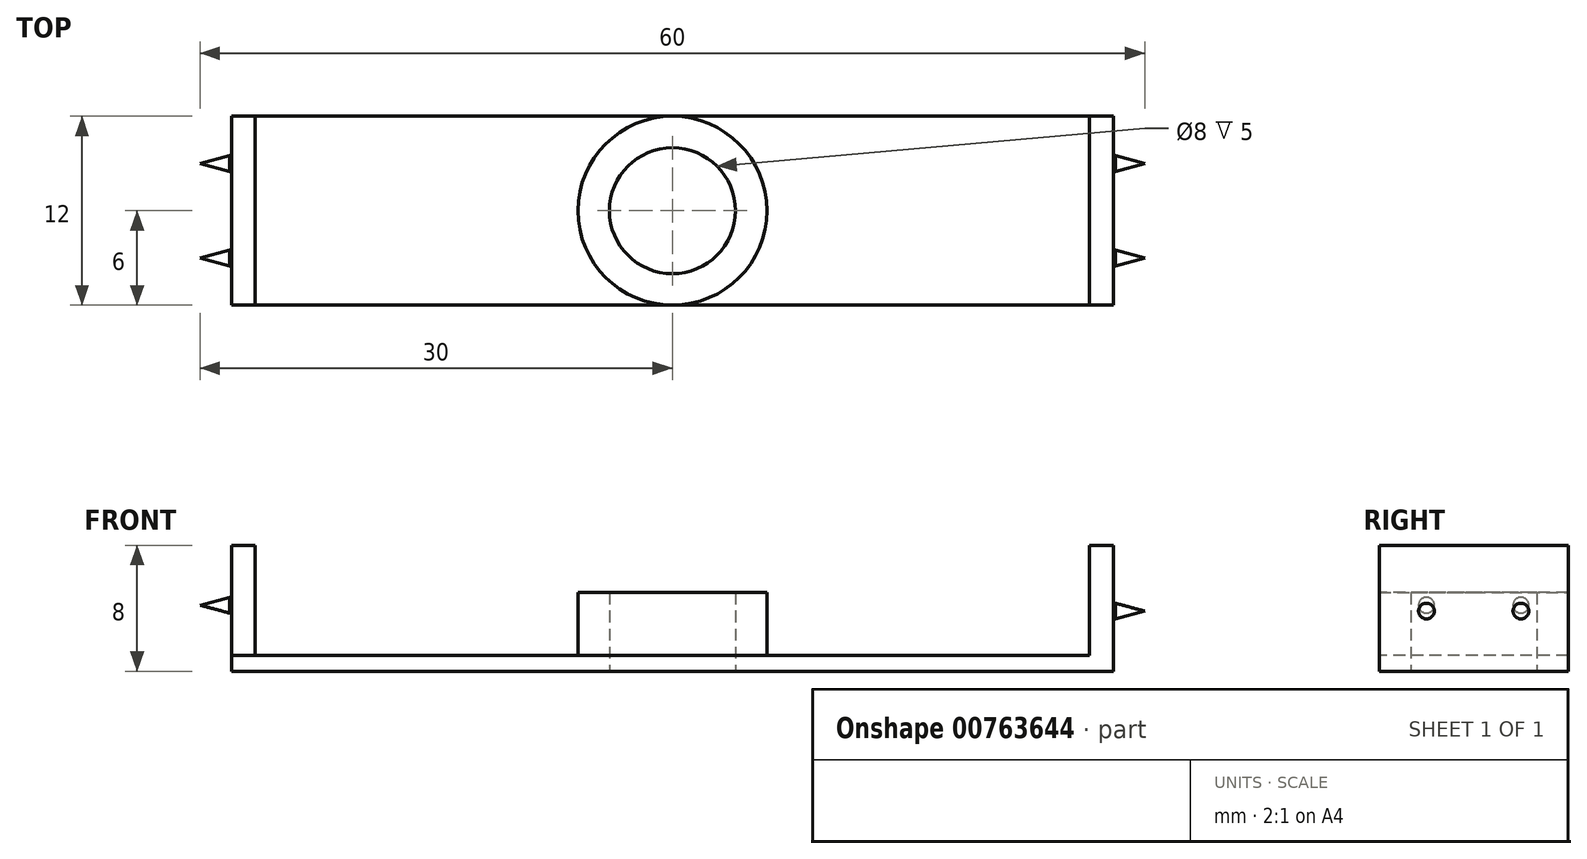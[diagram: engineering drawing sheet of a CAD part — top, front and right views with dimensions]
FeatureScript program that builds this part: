
annotation { "Feature Type Name" : "Feature", "Feature Type Description" : "" }
export const myFeature = defineFeature(function(context is Context, id is Id, definition is map)
    precondition{}
    {
        {
            var Q0;
            Q0=qCreatedBy(makeId("Top.planeOp"),FACE);
            var sketch = newSketch(context, id + "F0", { "sketchPlane" : qUnion([Q0])});
            skLineSegment(sketch, "E0.bottom", {"start": v(-28, 6) * mm, "end": v(28, 6) * mm});
            skLineSegment(sketch, "E0.top", {"start": v(-28, -6) * mm, "end": v(28, -6) * mm});
            skLineSegment(sketch, "E0.left", {"start": v(-28, 6) * mm, "end": v(-28, -6) * mm});
            skLineSegment(sketch, "E0.right", {"start": v(28, 6) * mm, "end": v(28, -6) * mm});
            skSolve(sketch);
        }
        {
            var Q0;
            Q0=makeQuery(id+"F0.imprint","IMPRINT",FACE,{"disambiguationData":[TD([[makeQuery(id+"F0.imprint","IMPRINT",EDGE,{"derivedFrom":sQuery(id+"F0.wireOp",EDGE,"E0.bottom")}),-1.0]])]});
            extrude(context, id + "F1", {"entities" : qUnion([Q0]), "depth" : 1 * mm, "offsetDistance" : 25 * mm});
        }
        {
            var Q0;
            Q0=makeQuery(id+"F1.opExtrude","CAP_FACE",FACE,{"disambiguationData":[OSD([sQuery(id+"F0.wireOp",EDGE,"E0.bottom"),sQuery(id+"F0.wireOp",EDGE,"E0.top"),sQuery(id+"F0.wireOp",EDGE,"E0.left"),sQuery(id+"F0.wireOp",EDGE,"E0.right")])],"isStart":false});
            var sketch = newSketch(context, id + "F2", { "sketchPlane" : qUnion([Q0])});
            skLineSegment(sketch, "E1.bottom", {"start": v(6, -6) * mm, "end": v(-6, -6) * mm});
            skLineSegment(sketch, "E1.top", {"start": v(6, 6) * mm, "end": v(-6, 6) * mm});
            skLineSegment(sketch, "E1.left", {"start": v(6, -6) * mm, "end": v(6, 6) * mm});
            skLineSegment(sketch, "E1.right", {"start": v(-6, -6) * mm, "end": v(-6, 6) * mm});
            skPoint(sketch, "E1.middle", {"position": v(0, 0) * mm});
            skCircle(sketch, "E2", {"center": v(0, 0) * mm, "radius": 4 * mm});
            skSolve(sketch);
        }
        {
            var Q0;
            Q0=makeQuery(id+"F2.imprint","IMPRINT",FACE,{"disambiguationData":[TD([[makeQuery(id+"F2.imprint","IMPRINT",EDGE,{"derivedFrom":sQuery(id+"F2.wireOp",EDGE,"E1.bottom")}),1.0]])]});
            extrude(context, id + "F3", {"entities" : qUnion([Q0]), "operationType" : NewBodyOperationType.ADD, "depth" : 4 * mm, "offsetDistance" : 25 * mm});
        }
        {
            var Q0;
            Q0=makeQuery(id+"F3.boolean.opBoolean","SPLIT",FACE,{"disambiguationData":[TD([makeQuery(id+"F3.opExtrude","SWEPT_FACE",FACE,{"disambiguationData":[OSD([sQuery(id+"F2.wireOp",EDGE,"E2")])]})])],"derivedFrom":makeQuery(id+"F1.opExtrude","CAP_FACE",FACE,{"disambiguationData":[OSD([sQuery(id+"F0.wireOp",EDGE,"E0.bottom"),sQuery(id+"F0.wireOp",EDGE,"E0.top"),sQuery(id+"F0.wireOp",EDGE,"E0.left"),sQuery(id+"F0.wireOp",EDGE,"E0.right")])],"isStart":false})});
            extrude(context, id + "F4", {"entities" : qUnion([Q0]), "operationType" : NewBodyOperationType.REMOVE, "oppositeDirection" : true, "depth" : 25 * mm, "offsetDistance" : 25 * mm});
        }
        {
            var Q0;
            Q0=makeQuery(id+"F3.opExtrude","SWEPT_EDGE",EDGE,{"disambiguationData":[OSD([sQuery(id+"F0.wireOp",EDGE,"E0.bottom"),sQuery(id+"F2.wireOp",EDGE,"E1.top"),sQuery(id+"F2.wireOp",EDGE,"E1.left")])]});
            var Q1;
            Q1=makeQuery(id+"F3.opExtrude","SWEPT_EDGE",EDGE,{"disambiguationData":[OSD([sQuery(id+"F0.wireOp",EDGE,"E0.top"),sQuery(id+"F2.wireOp",EDGE,"E1.bottom"),sQuery(id+"F2.wireOp",EDGE,"E1.left")])]});
            var Q2;
            Q2=makeQuery(id+"F3.opExtrude","SWEPT_EDGE",EDGE,{"disambiguationData":[OSD([sQuery(id+"F0.wireOp",EDGE,"E0.top"),sQuery(id+"F2.wireOp",EDGE,"E1.bottom"),sQuery(id+"F2.wireOp",EDGE,"E1.right")])]});
            var Q3;
            Q3=makeQuery(id+"F3.opExtrude","SWEPT_EDGE",EDGE,{"disambiguationData":[OSD([sQuery(id+"F0.wireOp",EDGE,"E0.bottom"),sQuery(id+"F2.wireOp",EDGE,"E1.top"),sQuery(id+"F2.wireOp",EDGE,"E1.right")])]});
            fillet(context, id + "F5", {"entities" : qUnion([Q0, Q1, Q2, Q3]), "radius" : 6 * mm, "tangentPropagation" : true, "allowEdgeOverflow" : false});
        }
        {
            var Q0;
            Q0=makeQuery(id+"F1.opExtrude","SWEPT_FACE",FACE,{"disambiguationData":[OSD([sQuery(id+"F0.wireOp",EDGE,"E0.right")])]});
            var sketch = newSketch(context, id + "F6", { "sketchPlane" : qUnion([Q0])});
            skLineSegment(sketch, "E3.bottom", {"start": v(-6, 0) * mm, "end": v(6, 0) * mm});
            skLineSegment(sketch, "E3.top", {"start": v(-6, 8) * mm, "end": v(6, 8) * mm});
            skLineSegment(sketch, "E3.left", {"start": v(-6, 0) * mm, "end": v(-6, 8) * mm});
            skLineSegment(sketch, "E3.right", {"start": v(6, 0) * mm, "end": v(6, 8) * mm});
            skSolve(sketch);
        }
        {
            var Q0;
            {var subQ0=sQuery(id+"F6.wireOp",EDGE,"E3.top");Q0=makeQuery(id+"F6.imprint","IMPRINT",FACE,{"disambiguationData":[TD([[makeQuery(id+"F6.imprint","IMPRINT",EDGE,{"derivedFrom":subQ0}),-1.0]])]});}
            extrude(context, id + "F7", {"entities" : qUnion([Q0]), "operationType" : NewBodyOperationType.ADD, "oppositeDirection" : true, "depth" : 1.5 * mm, "offsetDistance" : 25 * mm});
        }
        {
            var Q0;
            Q0=makeQuery(id+"F1.opExtrude","SWEPT_FACE",FACE,{"disambiguationData":[OSD([sQuery(id+"F0.wireOp",EDGE,"E0.left")])]});
            var sketch = newSketch(context, id + "F8", { "sketchPlane" : qUnion([Q0])});
            skLineSegment(sketch, "E4.bottom", {"start": v(6, 0) * mm, "end": v(-6, 0) * mm});
            skLineSegment(sketch, "E4.top", {"start": v(6, 8) * mm, "end": v(-6, 8) * mm});
            skLineSegment(sketch, "E4.left", {"start": v(6, 0) * mm, "end": v(6, 8) * mm});
            skLineSegment(sketch, "E4.right", {"start": v(-6, 0) * mm, "end": v(-6, 8) * mm});
            skSolve(sketch);
        }
        {
            var Q0;
            {var subQ0=sQuery(id+"F8.wireOp",EDGE,"E4.top");Q0=makeQuery(id+"F8.imprint","IMPRINT",FACE,{"disambiguationData":[TD([[makeQuery(id+"F8.imprint","IMPRINT",EDGE,{"derivedFrom":subQ0}),1.0]])]});}
            extrude(context, id + "F9", {"entities" : qUnion([Q0]), "oppositeDirection" : true, "depth" : 1.5 * mm, "offsetDistance" : 25 * mm});
        }
        {
            var Q0;
            {var subQ0=sQuery(id+"F0.wireOp",EDGE,"E0.right");Q0=makeQuery(id+"F7.boolean.opBoolean","MERGE",FACE,{"derivedFrom":[makeQuery(id+"F1.opExtrude","SWEPT_FACE",FACE,{"disambiguationData":[OSD([subQ0])]}),makeQuery(id+"F7.opExtrude","CAP_FACE",FACE,{"disambiguationData":[OSD([subQ0,sQuery(id+"F6.wireOp",EDGE,"E3.top"),sQuery(id+"F6.wireOp",EDGE,"E3.left"),sQuery(id+"F6.wireOp",EDGE,"E3.right")])],"isStart":true})]});}
            var sketch = newSketch(context, id + "F10", { "sketchPlane" : qUnion([Q0])});
            skCircle(sketch, "E5", {"center": v(3, 3.82) * mm, "radius": 0.5 * mm});
            skCircle(sketch, "E6.1.0.0", {"center": v(-3, 3.82) * mm, "radius": 0.5 * mm});
            skLineSegment(sketch, "E6.direction1", {"start": v(3, 3.82) * mm, "end": v(-3, 3.82) * mm, "construction": true});
            skSolve(sketch);
        }
        {
            var Q0;
            Q0=makeQuery(id+"F10.imprint","IMPRINT",FACE,{"disambiguationData":[TD([[makeQuery(id+"F10.imprint","IMPRINT",EDGE,{"derivedFrom":sQuery(id+"F10.wireOp",EDGE,"E5")}),1.0]])]});
            var Q1;
            Q1=makeQuery(id+"F10.imprint","IMPRINT",FACE,{"disambiguationData":[TD([[makeQuery(id+"F10.imprint","IMPRINT",EDGE,{"derivedFrom":sQuery(id+"F10.wireOp",EDGE,"E6.1.0.0")}),1.0]])]});
            extrude(context, id + "F11", {"entities" : qUnion([Q0, Q1]), "operationType" : NewBodyOperationType.ADD, "depth" : 2 * mm, "offsetDistance" : 25 * mm});
        }
        {
            var Q0;
            Q0=makeQuery(id+"F9.opExtrude","CAP_FACE",FACE,{"disambiguationData":[OSD([sQuery(id+"F0.wireOp",EDGE,"E0.left"),sQuery(id+"F8.wireOp",EDGE,"E4.top"),sQuery(id+"F8.wireOp",EDGE,"E4.left"),sQuery(id+"F8.wireOp",EDGE,"E4.right")])],"isStart":true});
            var sketch = newSketch(context, id + "F12", { "sketchPlane" : qUnion([Q0])});
            skCircle(sketch, "E7", {"center": v(3, 4.2) * mm, "radius": 0.5 * mm});
            skCircle(sketch, "E8.1.0.0", {"center": v(-3, 4.2) * mm, "radius": 0.5 * mm});
            skLineSegment(sketch, "E8.direction1", {"start": v(3, 4.2) * mm, "end": v(-3, 4.2) * mm, "construction": true});
            skSolve(sketch);
        }
        {
            var Q0;
            Q0=makeQuery(id+"F12.imprint","IMPRINT",FACE,{"disambiguationData":[TD([[makeQuery(id+"F12.imprint","IMPRINT",EDGE,{"derivedFrom":sQuery(id+"F12.wireOp",EDGE,"E7")}),1.0]])]});
            var Q1;
            Q1=makeQuery(id+"F12.imprint","IMPRINT",FACE,{"disambiguationData":[TD([[makeQuery(id+"F12.imprint","IMPRINT",EDGE,{"derivedFrom":sQuery(id+"F12.wireOp",EDGE,"E8.1.0.0")}),1.0]])]});
            extrude(context, id + "F13", {"entities" : qUnion([Q0, Q1]), "operationType" : NewBodyOperationType.ADD, "depth" : 2 * mm, "offsetDistance" : 25 * mm});
        }
        {
            var Q0;
            Q0=makeQuery(id+"F11.opExtrude","CAP_EDGE",EDGE,{"disambiguationData":[OSD([sQuery(id+"F10.wireOp",EDGE,"E5")])],"isStart":false});
            var Q1;
            Q1=makeQuery(id+"F11.opExtrude","CAP_EDGE",EDGE,{"disambiguationData":[OSD([sQuery(id+"F10.wireOp",EDGE,"E6.1.0.0")])],"isStart":false});
            var Q2;
            Q2=makeQuery(id+"F13.opExtrude","CAP_EDGE",EDGE,{"disambiguationData":[OSD([sQuery(id+"F12.wireOp",EDGE,"E7")])],"isStart":false});
            var Q3;
            Q3=makeQuery(id+"F13.opExtrude","CAP_EDGE",EDGE,{"disambiguationData":[OSD([sQuery(id+"F12.wireOp",EDGE,"E8.1.0.0")])],"isStart":false});
            chamfer(context, id + "F14", {"entities" : qUnion([Q0, Q1, Q2, Q3]), "chamferType" : ChamferType.OFFSET_ANGLE, "width" : .5 * mm, "oppositeDirection" : false, "angle" : 75 * degree, "tangentPropagation" : true});
        }
    });
